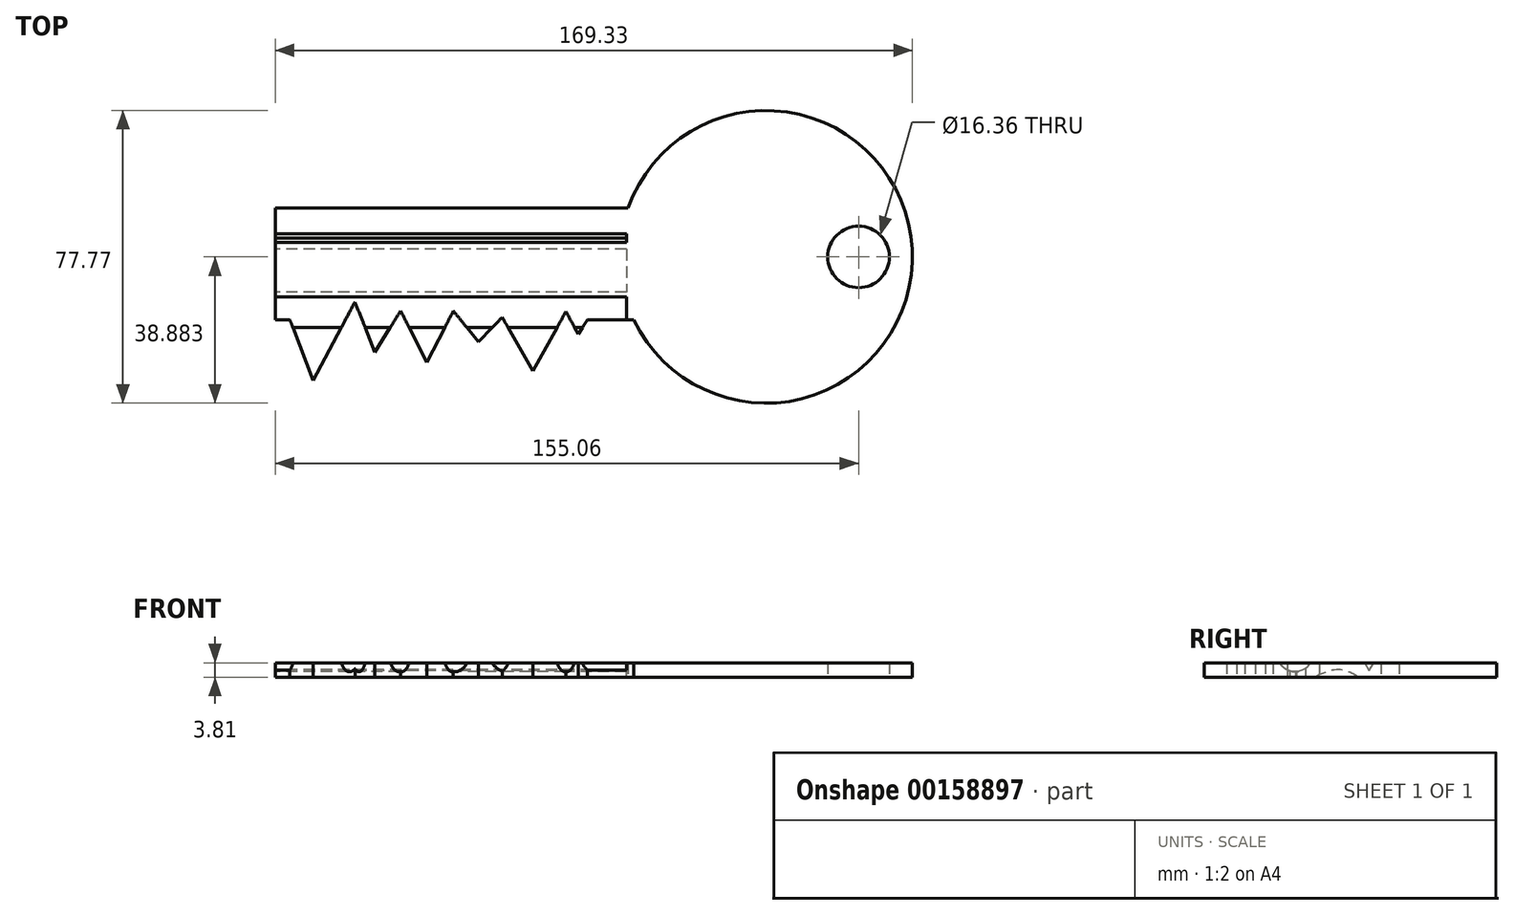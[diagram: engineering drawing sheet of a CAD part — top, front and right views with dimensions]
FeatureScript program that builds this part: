
annotation { "Feature Type Name" : "Feature", "Feature Type Description" : "" }
export const myFeature = defineFeature(function(context is Context, id is Id, definition is map)
    precondition{}
    {
        {
            var Q0;
            Q0=qCreatedBy(makeId("Top.planeOp"),FACE);
            var sketch = newSketch(context, id + "F0", { "sketchPlane" : qUnion([Q0])});
            skArc(sketch, "E0", {"start": v(9.7, -12.65) * mm, "mid": v(83.62, 6.14) * mm, "end": v(8.14, 17.1) * mm});
            skLineSegment(sketch, "E1.bottom", {"start": v(8.14, 17.1) * mm, "end": v(-85.65, 17.1) * mm});
            skLineSegment(sketch, "E1.top", {"start": v(9.7, -12.65) * mm, "end": v(-2.69, -12.65) * mm});
            skLineSegment(sketch, "E1.right", {"start": v(-85.65, 17.1) * mm, "end": v(-85.65, -12.65) * mm});
            skCircle(sketch, "E2", {"center": v(69.41, 4.1) * mm, "radius": 8.18 * mm});
            skLineSegment(sketch, "E3", {"start": v(-81.73, -12.65) * mm, "end": v(-75.56, -28.72) * mm});
            skLineSegment(sketch, "E4", {"start": v(-75.56, -28.72) * mm, "end": v(-64.45, -7.86) * mm});
            skLineSegment(sketch, "E5", {"start": v(-64.45, -7.86) * mm, "end": v(-59.15, -21.2) * mm});
            skLineSegment(sketch, "E6", {"start": v(-59.15, -21.2) * mm, "end": v(-52.31, -10.26) * mm});
            skLineSegment(sketch, "E7", {"start": v(-52.31, -10.26) * mm, "end": v(-45.3, -23.93) * mm});
            skLineSegment(sketch, "E8", {"start": v(-45.3, -23.93) * mm, "end": v(-38.3, -10.26) * mm});
            skLineSegment(sketch, "E9", {"start": v(-38.3, -10.26) * mm, "end": v(-31.63, -18.46) * mm});
            skLineSegment(sketch, "E10", {"start": v(-31.63, -18.46) * mm, "end": v(-25.3, -11.97) * mm});
            skLineSegment(sketch, "E11", {"start": v(-25.3, -11.97) * mm, "end": v(-17.1, -26.16) * mm});
            skLineSegment(sketch, "E12", {"start": v(-17.1, -26.16) * mm, "end": v(-8.38, -10.43) * mm});
            skLineSegment(sketch, "E13", {"start": v(-8.38, -10.43) * mm, "end": v(-5.13, -16.41) * mm});
            skLineSegment(sketch, "E14", {"start": v(-5.13, -16.41) * mm, "end": v(-2.69, -12.65) * mm});
            skLineSegment(sketch, "E15.trimOffspring", {"start": v(-24.9, -12.65) * mm, "end": v(-25.97, -12.65) * mm});
            skLineSegment(sketch, "E16.trimOffspring", {"start": v(-81.73, -12.65) * mm, "end": v(-85.65, -12.65) * mm});
            skPoint(sketch, "E17", {"position": v(30, -5.08) * mm});
            skSolve(sketch);
        }
        {
            var Q0;
            Q0=makeQuery(id+"F0.imprint","IMPRINT",FACE,{"disambiguationData":[TD([[makeQuery(id+"F0.imprint","IMPRINT",EDGE,{"derivedFrom":sQuery(id+"F0.wireOp",EDGE,"E0")}),1.0]])]});
            extrude(context, id + "F1", {"entities" : qUnion([Q0]), "depth" : 3.8 * mm});
        }
        {
            var Q0;
            Q0=makeQuery(id+"F1.opExtrude","SWEPT_FACE",FACE,{"disambiguationData":[OSD([sQuery(id+"F0.wireOp",EDGE,"E1.right")])]});
            var sketch = newSketch(context, id + "F2", { "sketchPlane" : qUnion([Q0])});
            skCircle(sketch, "E18.cCircle", {"center": v(-9.12, 8.3) * mm, "radius": 3.25 * mm, "construction": true});
            skLineSegment(sketch, "E18.0", {"start": v(-3.5, 11.54) * mm, "end": v(-9.12, 1.8) * mm});
            skLineSegment(sketch, "E18.1", {"start": v(-9.12, 1.8) * mm, "end": v(-14.75, 11.54) * mm});
            skLineSegment(sketch, "E18.2", {"start": v(-14.75, 11.54) * mm, "end": v(-3.5, 11.54) * mm});
            skPoint(sketch, "E18.0.midPoint", {"position": v(-6.3, 6.67) * mm});
            skCircle(sketch, "E19", {"center": v(10.6, 6.1) * mm, "radius": 4.67 * mm});
            skFitSpline(sketch, "E20", {"points": [v(-6.12, -0.75) * mm, v(-4.78, 0.92) * mm, v(1.7, 1.6) * mm, v(7.68, -2.85) * mm, v(-6.12, -0.75) * mm]});
            skSolve(sketch);
        }
        {
            var Q0;
            {var subQ0=sQuery(id+"F2.wireOp",EDGE,"E18.1");var subQ1=sQuery(id+"F2.wireOp",EDGE,"E18.0");var subQ2=makeQuery(id+"F2.imprint","INTERSECT",VERTEX,{"derivedFrom":[subQ1,subQ0]});Q0=makeQuery(id+"F2.imprint","IMPRINT",FACE,{"disambiguationData":[TD([[makeQuery(id+"F2.imprint","IMPRINT",EDGE,{"disambiguationData":[TD([[subQ2,1.0]])],"derivedFrom":subQ1}),-1.0]])]});}
            var Q1;
            {var subQ0=sQuery(id+"F2.wireOp",EDGE,"E19");var subQ1=sQuery(id+"F0.wireOp",EDGE,"E1.right");var subQ4=makeQuery(id+"F1.opExtrude","CAP_EDGE",EDGE,{"disambiguationData":[OSD([subQ1])],"isStart":false});var subQ5=makeQuery(id+"F2.imprint","INTERSECT",VERTEX,{"derivedFrom":[subQ4,subQ0]});Q1=makeQuery(id+"F2.imprint","IMPRINT",FACE,{"disambiguationData":[TD([[makeQuery(id+"F2.imprint","IMPRINT",EDGE,{"disambiguationData":[TD([[subQ5,-1.0]])],"derivedFrom":subQ0}),1.0]])]});}
            var Q2;
            {var subQ0=sQuery(id+"F2.wireOp",EDGE,"E20");var subQ1=makeQuery(id+"F1.opExtrude","CAP_EDGE",EDGE,{"disambiguationData":[OSD([sQuery(id+"F0.wireOp",EDGE,"E1.right")])],"isStart":true});var subQ2=makeQuery(id+"F2.imprint","INTERSECT",VERTEX,{"disambiguationData":[OD(0.0)],"derivedFrom":[subQ1,subQ0]});Q2=makeQuery(id+"F2.imprint","IMPRINT",FACE,{"disambiguationData":[TD([[makeQuery(id+"F2.imprint","IMPRINT",EDGE,{"disambiguationData":[TD([[subQ2,-1.0]])],"derivedFrom":subQ0}),-1.0]])]});}
            var Q3;
            {var subQ0=sQuery(id+"F2.wireOp",EDGE,"E19");var subQ1=sQuery(id+"F0.wireOp",EDGE,"E1.right");var subQ4=makeQuery(id+"F1.opExtrude","CAP_EDGE",EDGE,{"disambiguationData":[OSD([subQ1])],"isStart":false});var subQ5=makeQuery(id+"F2.imprint","INTERSECT",VERTEX,{"derivedFrom":[subQ4,subQ0]});Q3=makeQuery(id+"F2.imprint","IMPRINT",FACE,{"disambiguationData":[TD([[makeQuery(id+"F2.imprint","IMPRINT",EDGE,{"disambiguationData":[TD([[subQ5,1.0]])],"derivedFrom":subQ0}),1.0]])]});}
            var Q4;
            {var subQ0=sQuery(id+"F2.wireOp",EDGE,"E18.2");Q4=makeQuery(id+"F2.imprint","IMPRINT",FACE,{"disambiguationData":[TD([[makeQuery(id+"F2.imprint","IMPRINT",EDGE,{"derivedFrom":subQ0}),-1.0]])]});}
            var Q5;
            {var subQ0=sQuery(id+"F2.wireOp",EDGE,"E20");var subQ1=makeQuery(id+"F1.opExtrude","CAP_EDGE",EDGE,{"disambiguationData":[OSD([sQuery(id+"F0.wireOp",EDGE,"E1.right")])],"isStart":true});var subQ2=makeQuery(id+"F2.imprint","INTERSECT",VERTEX,{"disambiguationData":[OD(0.0)],"derivedFrom":[subQ1,subQ0]});Q5=makeQuery(id+"F2.imprint","IMPRINT",FACE,{"disambiguationData":[TD([[makeQuery(id+"F2.imprint","IMPRINT",EDGE,{"disambiguationData":[TD([[subQ2,1.0]])],"derivedFrom":subQ0}),-1.0]])]});}
            extrude(context, id + "F3", {"entities" : qUnion([Q0, Q1, Q2, Q3, Q4, Q5]), "operationType" : NewBodyOperationType.REMOVE, "oppositeDirection" : true, "depth" : 93.34 * mm});
        }
    });
